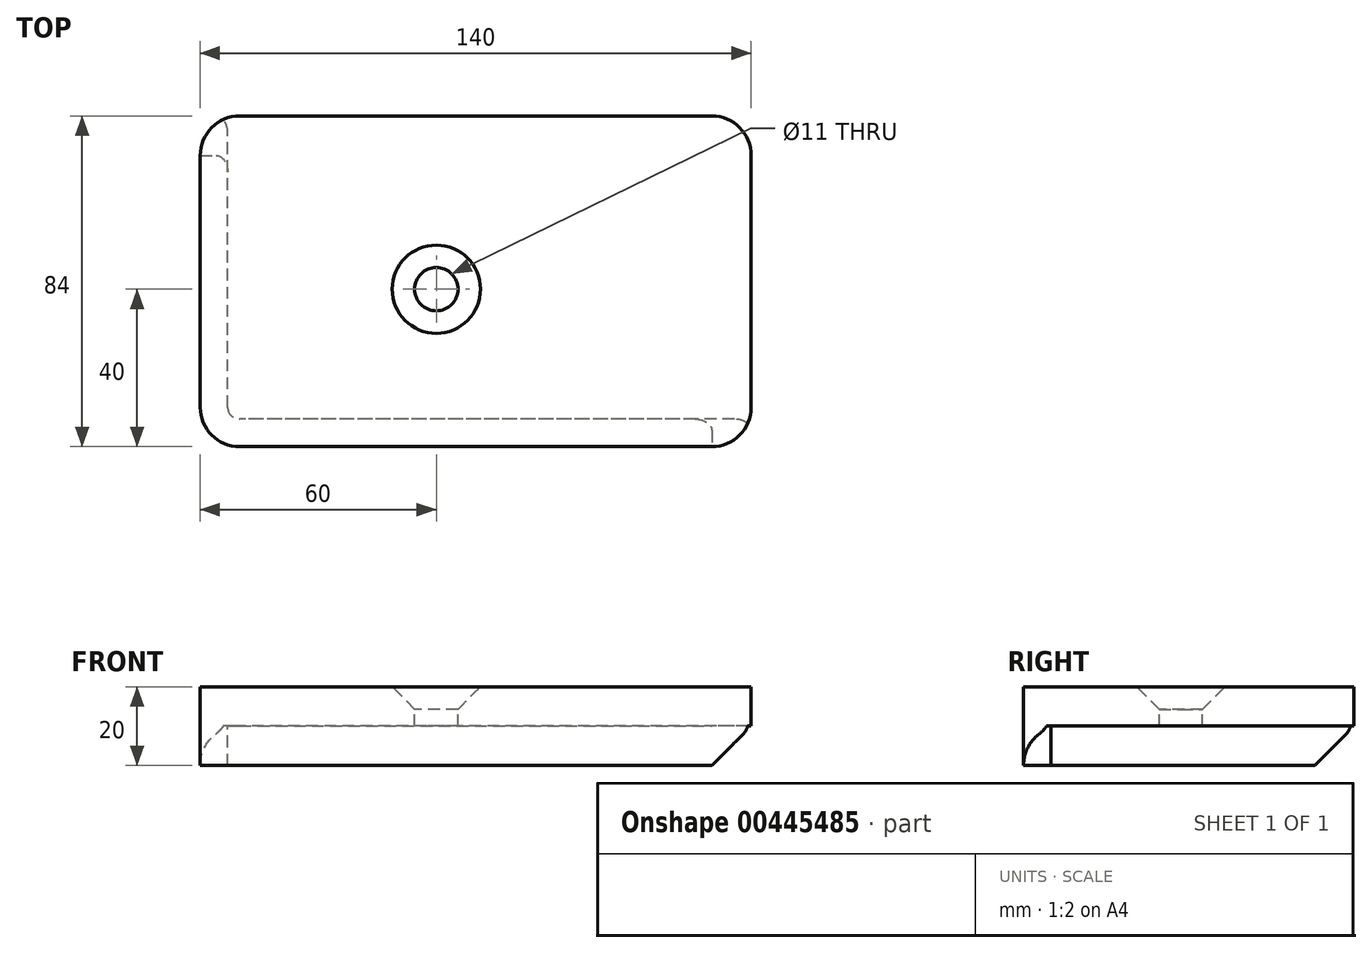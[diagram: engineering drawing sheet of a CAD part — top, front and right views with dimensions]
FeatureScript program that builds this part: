
annotation { "Feature Type Name" : "Feature", "Feature Type Description" : "" }
export const myFeature = defineFeature(function(context is Context, id is Id, definition is map)
    precondition{}
    {
        {
            var Q0;
            Q0=qCreatedBy(makeId("Top.planeOp"),FACE);
            var sketch = newSketch(context, id + "F0", { "sketchPlane" : qUnion([Q0])});
            skLineSegment(sketch, "E0.bottom", {"start": v(-60, 44) * mm, "end": v(80, 44) * mm});
            skLineSegment(sketch, "E0.top", {"start": v(-60, -40) * mm, "end": v(80, -40) * mm});
            skLineSegment(sketch, "E0.left", {"start": v(-60, 44) * mm, "end": v(-60, -40) * mm});
            skLineSegment(sketch, "E0.right", {"start": v(80, 44) * mm, "end": v(80, -40) * mm});
            skPoint(sketch, "E1", {"position": v(0, 0) * mm});
            skSolve(sketch);
        }
        {
            var Q0;
            Q0 = qSketchRegion(id + "F0", true);
            extrude(context, id + "F1", {"entities" : qUnion([Q0]), "oppositeDirection" : true, "depth" : 10 * mm});
        }
        {
            var Q0;
            Q0=sQuery(id+"F0.wireOp",VERTEX,"E1");
            var Q1;
            Q1=makeQuery(id+"F1.opExtrude","SWEPT_BODY",BODY,{"disambiguationData":[OSD([sQuery(id+"F0.wireOp",EDGE,"E0.bottom"),sQuery(id+"F0.wireOp",EDGE,"E0.top"),sQuery(id+"F0.wireOp",EDGE,"E0.left"),sQuery(id+"F0.wireOp",EDGE,"E0.right")])]});
            hole(context, id + "F2", {"style" : HoleStyle.C_SINK, "endStyle" : HoleEndStyle.BLIND, "standardTappedOrClearance" : lookupTablePath({ "standard" : "ISO", "fit" : "Normal", "size" : "M10", "type" : "Clearance" }), "standardBlindInLast" : lookupTablePath({ "fit" : "Standard", "standard" : "ISO", "size" : "M10", "type" : "Clearance" }), "holeDiameter" : 11 * mm, "cSinkDiameter" : 22.4 * mm, "cSinkAngle" : 90 * degree, "holeDepth" : 30 * mm, "isTappedThrough" : true, "tappedDepth" : 7 * mm, "tapClearance" : 6, "startFromSketch" : true, "locations" : qUnion([Q0]), "scope" : qUnion([Q1])});
        }
        {
            var Q0;
            Q0=makeQuery(id+"F1.opExtrude","CAP_FACE",FACE,{"disambiguationData":[OSD([sQuery(id+"F0.wireOp",EDGE,"E0.bottom"),sQuery(id+"F0.wireOp",EDGE,"E0.top"),sQuery(id+"F0.wireOp",EDGE,"E0.left"),sQuery(id+"F0.wireOp",EDGE,"E0.right")])],"isStart":false});
            var sketch = newSketch(context, id + "F3", { "sketchPlane" : qUnion([Q0])});
            skLineSegment(sketch, "E2", {"start": v(-60, 40) * mm, "end": v(80, 40) * mm});
            skLineSegment(sketch, "E3", {"start": v(80, 40) * mm, "end": v(80, 33) * mm});
            skLineSegment(sketch, "E4", {"start": v(80, 33) * mm, "end": v(-53, 33) * mm});
            skLineSegment(sketch, "E5", {"start": v(-53, 33) * mm, "end": v(-53, -44) * mm});
            skLineSegment(sketch, "E6", {"start": v(-53, -44) * mm, "end": v(-60, -44) * mm});
            skLineSegment(sketch, "E7", {"start": v(-60, -44) * mm, "end": v(-60, 40) * mm});
            skSolve(sketch);
        }
        {
            var Q0;
            Q0 = qSketchRegion(id + "F3", true);
            extrude(context, id + "F4", {"entities" : qUnion([Q0]), "operationType" : NewBodyOperationType.ADD, "depth" : 10 * mm});
        }
        {
            var Q0;
            Q0=makeQuery(id+"F4.opExtrude","CAP_EDGE",EDGE,{"disambiguationData":[OSD([sQuery(id+"F3.wireOp",EDGE,"E6")])],"isStart":false});
            var Q1;
            Q1=makeQuery(id+"F4.opExtrude","CAP_EDGE",EDGE,{"disambiguationData":[OSD([sQuery(id+"F3.wireOp",EDGE,"E3")])],"isStart":false});
            chamfer(context, id + "F5", {"entities" : qUnion([Q0, Q1]), "width" : 10 * mm, "tangentPropagation" : true});
        }
        {
            var Q0;
            Q0=makeQuery(id+"F4.boolean.opBoolean","MERGE",EDGE,{"derivedFrom":[makeQuery(id+"F1.opExtrude","SWEPT_EDGE",EDGE,{"disambiguationData":[OSD([sQuery(id+"F0.wireOp",EDGE,"E0.top"),sQuery(id+"F0.wireOp",EDGE,"E0.left")])]}),makeQuery(id+"F4.opExtrude","SWEPT_EDGE",EDGE,{"disambiguationData":[OSD([sQuery(id+"F3.wireOp",EDGE,"E2"),sQuery(id+"F3.wireOp",EDGE,"E7")])]})]});
            var Q1;
            Q1=makeQuery(id+"F4.boolean.opBoolean","MERGE",EDGE,{"derivedFrom":[makeQuery(id+"F1.opExtrude","SWEPT_EDGE",EDGE,{"disambiguationData":[OSD([sQuery(id+"F0.wireOp",EDGE,"E0.top"),sQuery(id+"F0.wireOp",EDGE,"E0.right")])]}),makeQuery(id+"F4.opExtrude","SWEPT_EDGE",EDGE,{"disambiguationData":[OSD([sQuery(id+"F3.wireOp",EDGE,"E2"),sQuery(id+"F3.wireOp",EDGE,"E3")])]})]});
            var Q2;
            Q2=makeQuery(id+"F1.opExtrude","SWEPT_EDGE",EDGE,{"disambiguationData":[OSD([sQuery(id+"F0.wireOp",EDGE,"E0.bottom"),sQuery(id+"F0.wireOp",EDGE,"E0.right")])]});
            var Q3;
            Q3=makeQuery(id+"F4.boolean.opBoolean","MERGE",EDGE,{"derivedFrom":[makeQuery(id+"F1.opExtrude","SWEPT_EDGE",EDGE,{"disambiguationData":[OSD([sQuery(id+"F0.wireOp",EDGE,"E0.bottom"),sQuery(id+"F0.wireOp",EDGE,"E0.left")])]}),makeQuery(id+"F4.opExtrude","SWEPT_EDGE",EDGE,{"disambiguationData":[OSD([sQuery(id+"F3.wireOp",EDGE,"E6"),sQuery(id+"F3.wireOp",EDGE,"E7")])]})]});
            fillet(context, id + "F6", {"entities" : qUnion([Q0, Q1, Q2, Q3]), "radius" : 10 * mm, "tangentPropagation" : true, "allowEdgeOverflow" : false});
        }
        {
            var Q0;
            Q0=makeQuery(id+"F4.opExtrude","SWEPT_EDGE",EDGE,{"disambiguationData":[OSD([sQuery(id+"F3.wireOp",EDGE,"E4"),sQuery(id+"F3.wireOp",EDGE,"E5")])]});
            var Q1;
            Q1=makeQuery(id+"F5.opChamfer","BLEND_EDGE",EDGE,{"blendedFrom":[makeQuery(id+"F4.opExtrude","CAP_EDGE",EDGE,{"disambiguationData":[OSD([sQuery(id+"F3.wireOp",EDGE,"E6")])],"isStart":false}),makeQuery(id+"F4.opExtrude","SWEPT_FACE",FACE,{"disambiguationData":[OSD([sQuery(id+"F3.wireOp",EDGE,"E5")])]})],"blendedInto":[makeQuery(id+"F4.opExtrude","SWEPT_FACE",FACE,{"disambiguationData":[OSD([sQuery(id+"F3.wireOp",EDGE,"E5")])]})]});
            var Q2;
            Q2=makeQuery(id+"F5.opChamfer","BLEND_EDGE",EDGE,{"blendedFrom":[makeQuery(id+"F4.opExtrude","CAP_EDGE",EDGE,{"disambiguationData":[OSD([sQuery(id+"F3.wireOp",EDGE,"E3")])],"isStart":false}),makeQuery(id+"F4.opExtrude","SWEPT_FACE",FACE,{"disambiguationData":[OSD([sQuery(id+"F3.wireOp",EDGE,"E4")])]})],"blendedInto":[makeQuery(id+"F4.opExtrude","SWEPT_FACE",FACE,{"disambiguationData":[OSD([sQuery(id+"F3.wireOp",EDGE,"E4")])]})]});
            var Q3;
            Q3=makeQuery(id+"F2.hole-0.boolean.opBoolean","COPY",EDGE,{"derivedFrom":makeQuery(id+"F2.hole-0.opRevolve","SWEPT_EDGE",EDGE,{"disambiguationData":[OSD([sQuery(id+"F2.hole-0.sketch.wireOp",EDGE,"csink_start_line_1"),sQuery(id+"F2.hole-0.sketch.wireOp",EDGE,"core_line_2")])]})});
            fillet(context, id + "F7", {"entities" : qUnion([Q0, Q1, Q2, Q3]), "radius" : 3 * mm, "tangentPropagation" : true, "allowEdgeOverflow" : false});
        }
    });
